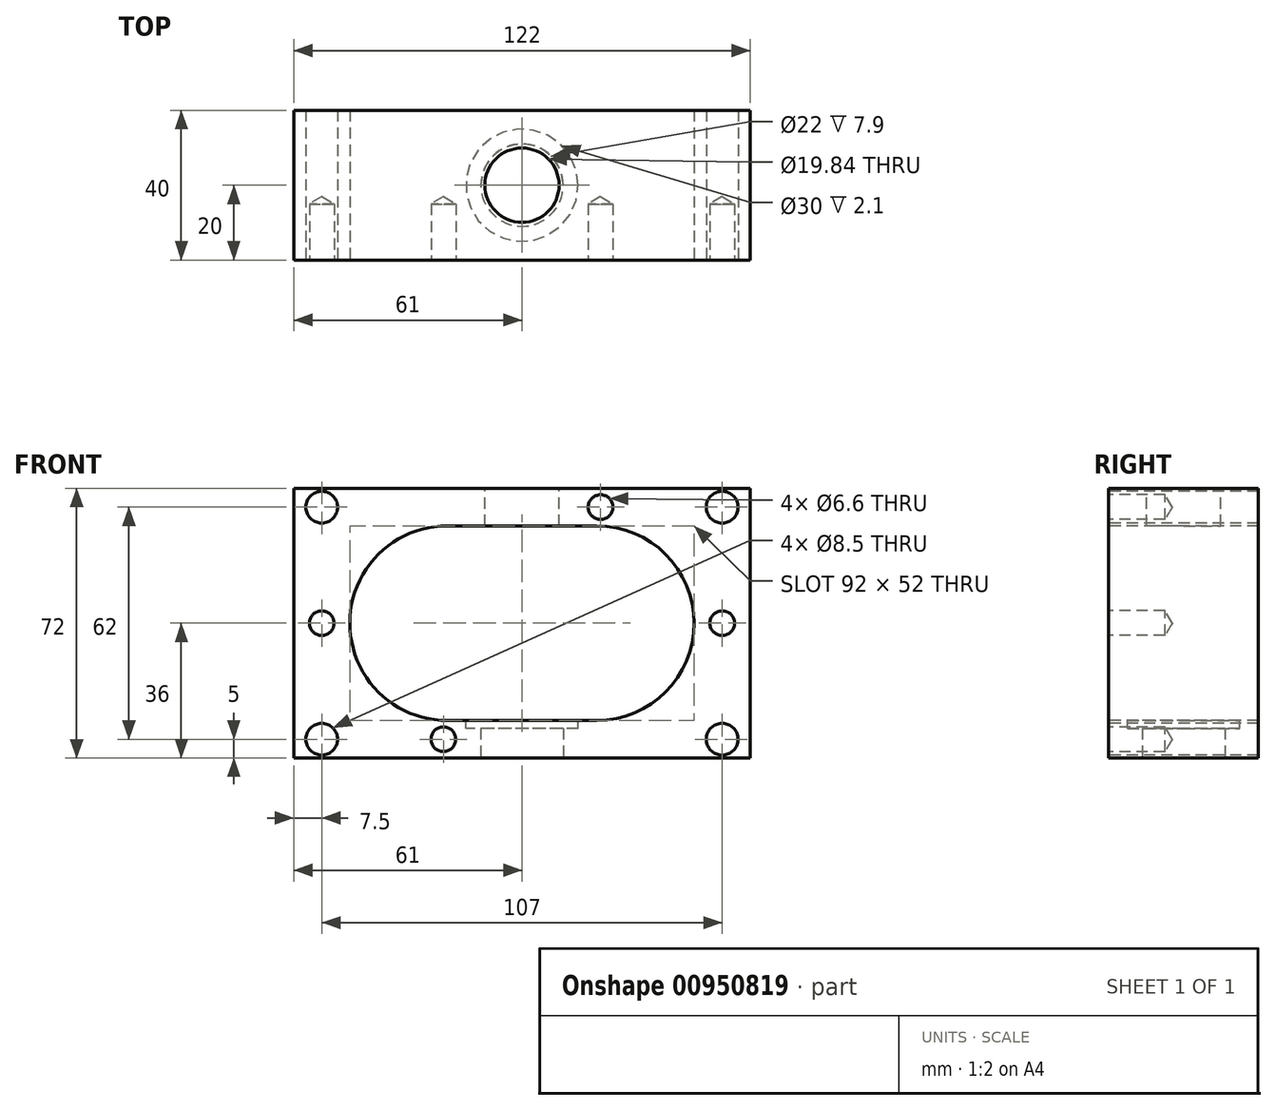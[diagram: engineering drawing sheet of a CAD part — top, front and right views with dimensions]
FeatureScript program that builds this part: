
annotation { "Feature Type Name" : "Feature", "Feature Type Description" : "" }
export const myFeature = defineFeature(function(context is Context, id is Id, definition is map)
    precondition{}
    {
        {
            var Q0;
            Q0=qCreatedBy(makeId("Front.planeOp"),FACE);
            var sketch = newSketch(context, id + "F0", { "sketchPlane" : qUnion([Q0])});
            skLineSegment(sketch, "E0.bottom", {"start": v(61, 36) * mm, "end": v(-61, 36) * mm});
            skLineSegment(sketch, "E0.top", {"start": v(61, -36) * mm, "end": v(-61, -36) * mm});
            skLineSegment(sketch, "E0.left", {"start": v(61, 36) * mm, "end": v(61, -36) * mm});
            skLineSegment(sketch, "E0.right", {"start": v(-61, 36) * mm, "end": v(-61, -36) * mm});
            skPoint(sketch, "E0.middle", {"position": v(0, 0) * mm});
            skArc(sketch, "E1", {"start": v(-20, 26) * mm, "mid": v(-46, -0.04) * mm, "end": v(-19.93, -26) * mm});
            skArc(sketch, "E2", {"start": v(20, -26) * mm, "mid": v(46, 0) * mm, "end": v(20, 26) * mm});
            skLineSegment(sketch, "E3", {"start": v(-20, 26) * mm, "end": v(20, 26) * mm});
            skLineSegment(sketch, "E4", {"start": v(-19.93, -26) * mm, "end": v(20, -26) * mm});
            skPoint(sketch, "E5", {"position": v(21, 31) * mm});
            skPoint(sketch, "E6", {"position": v(-21, -31) * mm});
            skPoint(sketch, "E7", {"position": v(53.5, 0) * mm});
            skPoint(sketch, "E8", {"position": v(-53.5, 0) * mm});
            skPoint(sketch, "E9", {"position": v(53.5, 31) * mm});
            skPoint(sketch, "E10", {"position": v(53.5, -31) * mm});
            skPoint(sketch, "E11", {"position": v(-53.5, -31) * mm});
            skPoint(sketch, "E12", {"position": v(-53.5, 31) * mm});
            skSolve(sketch);
        }
        {
            var Q0;
            Q0=qSketchRegion(id+"F0",true);
            extrude(context, id + "F1", {"entities" : qUnion([Q0]), "oppositeDirection" : true, "depth" : 40 * mm, "offsetDistance" : 25.4 * mm});
        }
        {
            var Q0;
            Q0=sQuery(id+"F0.wireOp",VERTEX,"E5");
            var Q1;
            Q1=sQuery(id+"F0.wireOp",VERTEX,"E7");
            var Q2;
            Q2=sQuery(id+"F0.wireOp",VERTEX,"E6");
            var Q3;
            Q3=sQuery(id+"F0.wireOp",VERTEX,"E8");
            var Q4;
            Q4=makeQuery(id+"F1.opExtrude","SWEPT_BODY",BODY,{"disambiguationData":[OSD([sQuery(id+"F0.wireOp",EDGE,"E0.bottom"),sQuery(id+"F0.wireOp",EDGE,"E0.top"),sQuery(id+"F0.wireOp",EDGE,"E0.left"),sQuery(id+"F0.wireOp",EDGE,"E0.right"),sQuery(id+"F0.wireOp",EDGE,"E1"),sQuery(id+"F0.wireOp",EDGE,"E2"),sQuery(id+"F0.wireOp",EDGE,"E3"),sQuery(id+"F0.wireOp",EDGE,"E4")])]});
            hole(context, id + "F2", {"style" : HoleStyle.SIMPLE, "endStyle" : HoleEndStyle.BLIND, "standardTappedOrClearance" : lookupTablePath({ "fit" : "Normal", "standard" : "ISO", "size" : "M6", "type" : "Clearance" }), "standardBlindInLast" : lookupTablePath({ "fit" : "Standard", "standard" : "ISO", "size" : "M6", "type" : "Clearance" }), "holeDiameter" : 6.6 * mm, "majorDiameter" : 6.35 * mm, "holeDepth" : 15 * mm, "isTappedThrough" : true, "tappedDepth" : 12.7 * mm, "tapClearance" : 3, "locations" : qUnion([Q0, Q1, Q2, Q3]), "scope" : qUnion([Q4])});
        }
        {
            var Q0;
            Q0=sQuery(id+"F0.wireOp",VERTEX,"E12");
            var Q1;
            Q1=sQuery(id+"F0.wireOp",VERTEX,"E11");
            var Q2;
            Q2=sQuery(id+"F0.wireOp",VERTEX,"E9");
            var Q3;
            Q3=sQuery(id+"F0.wireOp",VERTEX,"E10");
            var Q4;
            Q4=makeQuery(id+"F1.opExtrude","SWEPT_BODY",BODY,{"disambiguationData":[OSD([sQuery(id+"F0.wireOp",EDGE,"E0.bottom"),sQuery(id+"F0.wireOp",EDGE,"E0.top"),sQuery(id+"F0.wireOp",EDGE,"E0.left"),sQuery(id+"F0.wireOp",EDGE,"E0.right"),sQuery(id+"F0.wireOp",EDGE,"E1"),sQuery(id+"F0.wireOp",EDGE,"E2"),sQuery(id+"F0.wireOp",EDGE,"E3"),sQuery(id+"F0.wireOp",EDGE,"E4")])]});
            hole(context, id + "F3", {"style" : HoleStyle.SIMPLE, "endStyle" : HoleEndStyle.THROUGH, "standardTappedOrClearance" : lookupTablePath({ "standard" : "ISO", "size" : "8.5", "type" : "Drilled" }), "standardBlindInLast" : lookupTablePath({ "standard" : "ISO", "size" : "8.5", "type" : "Drilled" }), "holeDiameter" : 8.5 * mm, "majorDiameter" : 6.35 * mm, "isTappedThrough" : true, "tappedDepth" : 12.7 * mm, "tapClearance" : 3, "locations" : qUnion([Q0, Q1, Q2, Q3]), "scope" : qUnion([Q4])});
        }
        {
            var Q0;
            Q0=makeQuery(id+"F1.opExtrude","SWEPT_FACE",FACE,{"disambiguationData":[OSD([sQuery(id+"F0.wireOp",EDGE,"E0.bottom")])]});
            var sketch = newSketch(context, id + "F4", { "sketchPlane" : qUnion([Q0])});
            skPoint(sketch, "E13", {"position": v(0, 20) * mm});
            skSolve(sketch);
        }
        {
            var Q0;
            Q0=sQuery(id+"F4.wireOp",VERTEX,"E13");
            var Q1;
            Q1=makeQuery(id+"F1.opExtrude","SWEPT_BODY",BODY,{"disambiguationData":[OSD([sQuery(id+"F0.wireOp",EDGE,"E0.bottom"),sQuery(id+"F0.wireOp",EDGE,"E0.top"),sQuery(id+"F0.wireOp",EDGE,"E0.left"),sQuery(id+"F0.wireOp",EDGE,"E0.right"),sQuery(id+"F0.wireOp",EDGE,"E1"),sQuery(id+"F0.wireOp",EDGE,"E2"),sQuery(id+"F0.wireOp",EDGE,"E3"),sQuery(id+"F0.wireOp",EDGE,"E4")])]});
            hole(context, id + "F5", {"style" : HoleStyle.SIMPLE, "endStyle" : HoleEndStyle.BLIND, "standardTappedOrClearance" : lookupTablePath({ "fit" : "Normal (ASME)", "standard" : "ANSI", "size" : "3/4", "type" : "Clearance" }), "standardBlindInLast" : lookupTablePath({ "fit" : "Free", "standard" : "ANSI", "size" : "3/4", "type" : "Clearance" }), "holeDiameter" : 19.84 * mm, "majorDiameter" : 5 * mm, "holeDepth" : 15 * mm, "isTappedThrough" : true, "tappedDepth" : 12.7 * mm, "tapClearance" : 3, "locations" : qUnion([Q0]), "scope" : qUnion([Q1])});
        }
        {
            var Q0;
            Q0=makeQuery(id+"F1.opExtrude","SWEPT_FACE",FACE,{"disambiguationData":[OSD([sQuery(id+"F0.wireOp",EDGE,"E0.top")])]});
            var sketch = newSketch(context, id + "F6", { "sketchPlane" : qUnion([Q0])});
            skCircle(sketch, "E14", {"center": v(0, -20) * mm, "radius": 11 * mm});
            skSolve(sketch);
        }
        {
            var Q0;
            Q0=qSketchRegion(id+"F6",true);
            extrude(context, id + "F7", {"entities" : qUnion([Q0]), "operationType" : NewBodyOperationType.REMOVE, "oppositeDirection" : true, "depth" : 25 * mm, "offsetDistance" : 25 * mm});
        }
        {
            var Q0;
            Q0=makeQuery(id+"F1.opExtrude","SWEPT_FACE",FACE,{"disambiguationData":[OSD([sQuery(id+"F0.wireOp",EDGE,"E4")])]});
            var sketch = newSketch(context, id + "F8", { "sketchPlane" : qUnion([Q0])});
            skCircle(sketch, "E15", {"center": v(0, 20) * mm, "radius": 15 * mm});
            skSolve(sketch);
        }
        {
            var Q0;
            Q0=qSketchRegion(id+"F8",true);
            extrude(context, id + "F9", {"entities" : qUnion([Q0]), "operationType" : NewBodyOperationType.REMOVE, "oppositeDirection" : true, "depth" : 2.1 * mm, "offsetDistance" : 25 * mm});
        }
    });
